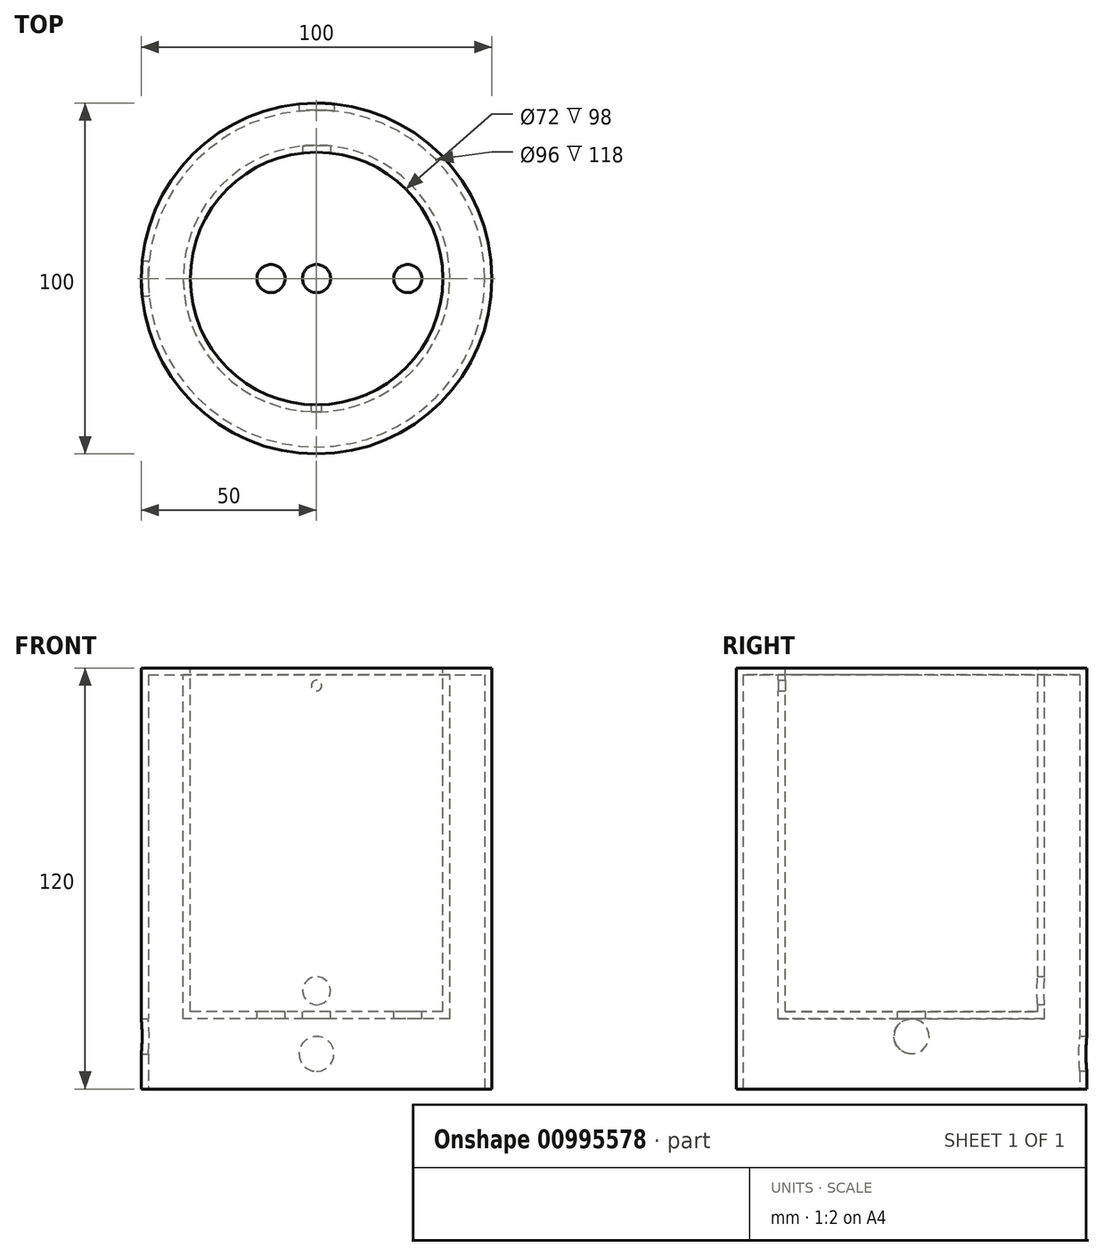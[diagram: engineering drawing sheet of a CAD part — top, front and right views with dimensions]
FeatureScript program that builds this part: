
annotation { "Feature Type Name" : "Feature", "Feature Type Description" : "" }
export const myFeature = defineFeature(function(context is Context, id is Id, definition is map)
    precondition{}
    {
        {
            var Q0;
            Q0=qCreatedBy(makeId("Top.planeOp"),FACE);
            var sketch = newSketch(context, id + "F0", { "sketchPlane" : qUnion([Q0])});
            skCircle(sketch, "E0", {"center": v(0, 0) * mm, "radius": 50 * mm});
            skSolve(sketch);
        }
        {
            var Q0;
            Q0 = qSketchRegion(id + "F0", true);
            extrude(context, id + "F1", {"entities" : qUnion([Q0]), "depth" : 120 * mm, "offsetDistance" : 25 * mm});
        }
        {
            var Q0;
            Q0=makeQuery(id+"F1.opExtrude","CAP_FACE",FACE,{"disambiguationData":[OSD([sQuery(id+"F0.wireOp",EDGE,"E0")])],"isStart":true});
            var sketch = newSketch(context, id + "F2", { "sketchPlane" : qUnion([Q0])});
            skCircle(sketch, "E1", {"center": v(0, 0) * mm, "radius": 48 * mm});
            skSolve(sketch);
        }
        {
            var Q0;
            Q0 = qSketchRegion(id + "F2", true);
            extrude(context, id + "F3", {"entities" : qUnion([Q0]), "operationType" : NewBodyOperationType.REMOVE, "oppositeDirection" : true, "depth" : 118 * mm, "offsetDistance" : 25 * mm});
        }
        {
            var Q0;
            Q0=makeQuery(id+"F1.opExtrude","CAP_FACE",FACE,{"disambiguationData":[OSD([sQuery(id+"F0.wireOp",EDGE,"E0")])],"isStart":false});
            var sketch = newSketch(context, id + "F4", { "sketchPlane" : qUnion([Q0])});
            skCircle(sketch, "E2", {"center": v(0, 0) * mm, "radius": 38 * mm});
            skSolve(sketch);
        }
        {
            var Q0;
            Q0 = qSketchRegion(id + "F4", true);
            extrude(context, id + "F5", {"entities" : qUnion([Q0]), "operationType" : NewBodyOperationType.ADD, "oppositeDirection" : true, "depth" : 100 * mm, "offsetDistance" : 25 * mm});
        }
        {
            var Q0;
            Q0=makeQuery(id+"F1.opExtrude","CAP_FACE",FACE,{"disambiguationData":[OSD([sQuery(id+"F0.wireOp",EDGE,"E0")])],"isStart":false});
            var sketch = newSketch(context, id + "F6", { "sketchPlane" : qUnion([Q0])});
            skCircle(sketch, "E3", {"center": v(0, 0) * mm, "radius": 36 * mm});
            skSolve(sketch);
        }
        {
            var Q0;
            Q0 = qSketchRegion(id + "F6", true);
            extrude(context, id + "F7", {"entities" : qUnion([Q0]), "operationType" : NewBodyOperationType.REMOVE, "oppositeDirection" : true, "depth" : 98 * mm, "offsetDistance" : 25 * mm});
        }
        {
            var Q0;
            Q0=qCreatedBy(makeId("Front.planeOp"),FACE);
            var sketch = newSketch(context, id + "F8", { "sketchPlane" : qUnion([Q0])});
            skCircle(sketch, "E4", {"center": v(0, 10) * mm, "radius": 5 * mm});
            skSolve(sketch);
        }
        {
            var Q0;
            Q0 = qSketchRegion(id + "F8", true);
            extrude(context, id + "F9", {"entities" : qUnion([Q0]), "operationType" : NewBodyOperationType.REMOVE, "endBound" : BoundingType.THROUGH_ALL, "oppositeDirection" : true, "depth" : 25 * mm, "offsetDistance" : 25 * mm});
        }
        {
            var Q0;
            Q0=qCreatedBy(makeId("Front.planeOp"),FACE);
            var sketch = newSketch(context, id + "F10", { "sketchPlane" : qUnion([Q0])});
            skLineSegment(sketch, "E5", {"start": v(0, 0) * mm, "end": v(0, 61.62) * mm, "construction": true});
            skSolve(sketch);
        }
        {
            var Q0;
            Q0=qCreatedBy(makeId("Right.planeOp"),FACE);
            var sketch = newSketch(context, id + "F11", { "sketchPlane" : qUnion([Q0])});
            skCircle(sketch, "E6", {"center": v(0, 15) * mm, "radius": 5 * mm});
            skSolve(sketch);
        }
        {
            var Q0;
            Q0 = qSketchRegion(id + "F11", true);
            extrude(context, id + "F12", {"entities" : qUnion([Q0]), "operationType" : NewBodyOperationType.REMOVE, "endBound" : BoundingType.THROUGH_ALL, "oppositeDirection" : true, "depth" : 25 * mm, "offsetDistance" : 25 * mm});
        }
        {
            var Q0;
            Q0=qCreatedBy(makeId("Front.planeOp"),FACE);
            var sketch = newSketch(context, id + "F13", { "sketchPlane" : qUnion([Q0])});
            skCircle(sketch, "E7", {"center": v(0, 115) * mm, "radius": 1.5 * mm});
            skSolve(sketch);
        }
        {
            var Q0;
            Q0 = qSketchRegion(id + "F13", true);
            var Q1;
            Q1=makeQuery(id+"F5.opExtrude","SWEPT_FACE",FACE,{"disambiguationData":[OSD([sQuery(id+"F4.wireOp",EDGE,"E2")])]});
            extrude(context, id + "F14", {"entities" : qUnion([Q0]), "operationType" : NewBodyOperationType.REMOVE, "endBound" : BoundingType.UP_TO_SURFACE, "depth" : 25 * mm, "endBoundEntityFace" : qUnion([Q1]), "offsetDistance" : 25 * mm});
        }
        {
            var Q0;
            Q0=qCreatedBy(makeId("Front.planeOp"),FACE);
            var sketch = newSketch(context, id + "F15", { "sketchPlane" : qUnion([Q0])});
            skCircle(sketch, "E8", {"center": v(0, 28) * mm, "radius": 4 * mm});
            skSolve(sketch);
        }
        {
            var Q0;
            Q0 = qSketchRegion(id + "F15", true);
            var Q1;
            Q1=makeQuery(id+"F5.opExtrude","SWEPT_FACE",FACE,{"disambiguationData":[OSD([sQuery(id+"F4.wireOp",EDGE,"E2")])]});
            extrude(context, id + "F16", {"entities" : qUnion([Q0]), "operationType" : NewBodyOperationType.REMOVE, "endBound" : BoundingType.UP_TO_SURFACE, "oppositeDirection" : true, "depth" : 25 * mm, "endBoundEntityFace" : qUnion([Q1]), "offsetDistance" : 25 * mm});
        }
        {
            var Q0;
            Q0=makeQuery(id+"F7.boolean.opBoolean","COPY",FACE,{"derivedFrom":makeQuery(id+"F7.opExtrude","CAP_FACE",FACE,{"disambiguationData":[OSD([sQuery(id+"F6.wireOp",EDGE,"E3")])],"isStart":false})});
            var sketch = newSketch(context, id + "F17", { "sketchPlane" : qUnion([Q0])});
            skCircle(sketch, "E9", {"center": v(0, 0) * mm, "radius": 4 * mm});
            skSolve(sketch);
        }
        {
            var Q0;
            Q0 = qSketchRegion(id + "F17", true);
            extrude(context, id + "F18", {"entities" : qUnion([Q0]), "operationType" : NewBodyOperationType.REMOVE, "endBound" : BoundingType.THROUGH_ALL, "oppositeDirection" : true, "depth" : 25 * mm, "offsetDistance" : 25 * mm});
        }
        {
            var Q0;
            Q0=makeQuery(id+"F17.imprint","IMPRINT",FACE,{"disambiguationData":[TD([[makeQuery(id+"F17.imprint","IMPRINT",EDGE,{"derivedFrom":sQuery(id+"F17.wireOp",EDGE,"E9")}),-1.0]])]});
            var sketch = newSketch(context, id + "F19", { "sketchPlane" : qUnion([Q0])});
            skCircle(sketch, "E10", {"center": v(-13, 0) * mm, "radius": 4 * mm});
            skSolve(sketch);
        }
        {
            var Q0;
            Q0 = qSketchRegion(id + "F19", true);
            extrude(context, id + "F20", {"entities" : qUnion([Q0]), "operationType" : NewBodyOperationType.REMOVE, "endBound" : BoundingType.THROUGH_ALL, "oppositeDirection" : true, "depth" : 25 * mm, "offsetDistance" : 25 * mm});
        }
        {
            var Q0;
            Q0=makeQuery(id+"F7.boolean.opBoolean","COPY",FACE,{"derivedFrom":makeQuery(id+"F7.opExtrude","CAP_FACE",FACE,{"disambiguationData":[OSD([sQuery(id+"F6.wireOp",EDGE,"E3")])],"isStart":false})});
            var sketch = newSketch(context, id + "F21", { "sketchPlane" : qUnion([Q0])});
            skCircle(sketch, "E11", {"center": v(26, 0) * mm, "radius": 4 * mm});
            skSolve(sketch);
        }
        {
            var Q0;
            Q0 = qSketchRegion(id + "F21", true);
            extrude(context, id + "F22", {"entities" : qUnion([Q0]), "operationType" : NewBodyOperationType.REMOVE, "endBound" : BoundingType.THROUGH_ALL, "oppositeDirection" : true, "depth" : 25 * mm, "offsetDistance" : 25 * mm});
        }
    });
